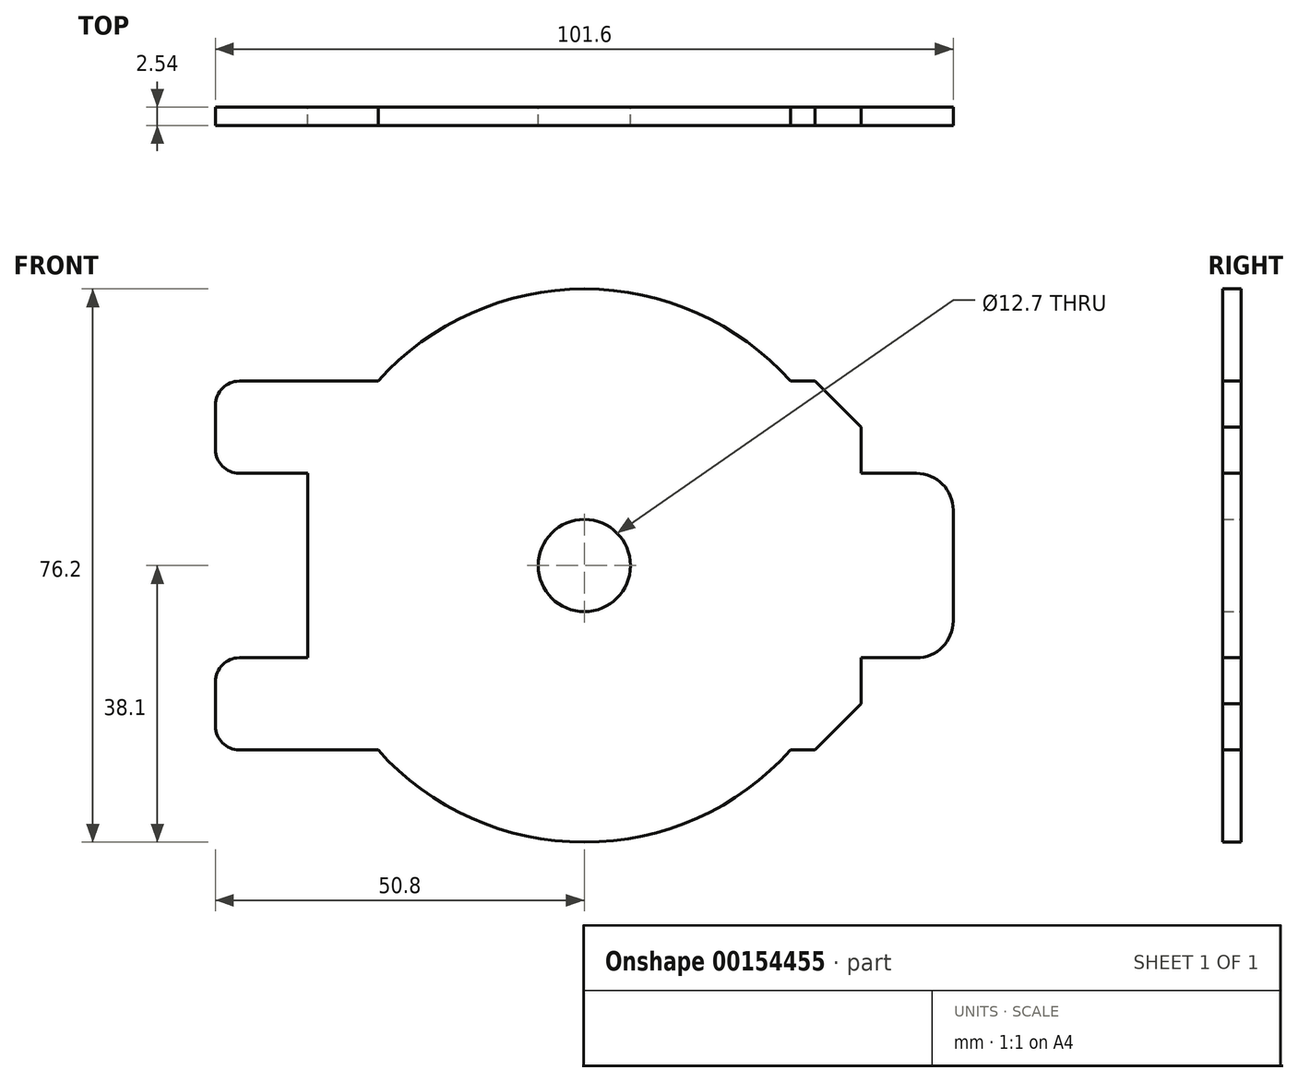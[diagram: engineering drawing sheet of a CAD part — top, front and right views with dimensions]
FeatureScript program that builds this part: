
annotation { "Feature Type Name" : "Feature", "Feature Type Description" : "" }
export const myFeature = defineFeature(function(context is Context, id is Id, definition is map)
    precondition{}
    {
        {
            var Q0;
            Q0=qCreatedBy(makeId("Front.planeOp"),FACE);
            var sketch = newSketch(context, id + "F0", { "sketchPlane" : qUnion([Q0])});
            skLineSegment(sketch, "E0.bottom", {"start": v(38.1, 25.4) * mm, "end": v(28.4, 25.4) * mm});
            skLineSegment(sketch, "E0.top", {"start": v(38.1, -25.4) * mm, "end": v(28.4, -25.4) * mm});
            skLineSegment(sketch, "E0.left", {"start": v(38.1, 25.4) * mm, "end": v(38.1, -25.4) * mm});
            skLineSegment(sketch, "E0.right", {"start": v(-38.1, 25.4) * mm, "end": v(-38.1, -25.4) * mm});
            skPoint(sketch, "E0.middle", {"position": v(0, 0) * mm});
            skArc(sketch, "E1", {"start": v(-28.4, -25.4) * mm, "mid": v(0, -38.1) * mm, "end": v(28.4, -25.4) * mm});
            skLineSegment(sketch, "E2.trimOffspring", {"start": v(-28.4, 25.4) * mm, "end": v(-38.1, 25.4) * mm});
            skLineSegment(sketch, "E3.trimOffspring", {"start": v(-28.4, -25.4) * mm, "end": v(-38.1, -25.4) * mm});
            skArc(sketch, "E4.trimOffspring", {"start": v(28.4, 25.4) * mm, "mid": v(0, 38.1) * mm, "end": v(-28.4, 25.4) * mm});
            skLineSegment(sketch, "E5.bottom", {"start": v(38.1, 12.7) * mm, "end": v(50.8, 12.7) * mm});
            skLineSegment(sketch, "E5.top", {"start": v(38.1, -12.7) * mm, "end": v(50.8, -12.7) * mm});
            skLineSegment(sketch, "E5.right", {"start": v(50.8, 12.7) * mm, "end": v(50.8, -12.7) * mm});
            skPoint(sketch, "E5.middle", {"position": v(38.1, 0) * mm});
            skPoint(sketch, "E5.left.start.orphan", {"position": v(25.4, 12.7) * mm});
            skPoint(sketch, "E6.orphan", {"position": v(25.4, -12.7) * mm});
            skPoint(sketch, "E7.MirrorCS.end.orphan", {"position": v(-25.4, -12.7) * mm});
            skPoint(sketch, "E7.MirrorCS.start.orphan", {"position": v(-25.4, 12.7) * mm});
            skPoint(sketch, "E8.MirrorCS.end.orphan", {"position": v(-50.8, 12.7) * mm});
            skPoint(sketch, "E9.MirrorCS.end.orphan", {"position": v(-50.8, -12.7) * mm});
            skLineSegment(sketch, "E10.bottom", {"start": v(-38.1, -25.4) * mm, "end": v(-50.8, -25.4) * mm});
            skLineSegment(sketch, "E10.top", {"start": v(-38.1, -12.7) * mm, "end": v(-50.8, -12.7) * mm});
            skLineSegment(sketch, "E10.left", {"start": v(-38.1, -25.4) * mm, "end": v(-38.1, -12.7) * mm});
            skLineSegment(sketch, "E10.right", {"start": v(-50.8, -25.4) * mm, "end": v(-50.8, -12.7) * mm});
            skLineSegment(sketch, "E11.MirrorCS", {"start": v(-38.1, 12.7) * mm, "end": v(-50.8, 12.7) * mm});
            skLineSegment(sketch, "E12.MirrorCS", {"start": v(-38.1, 25.4) * mm, "end": v(-50.8, 25.4) * mm});
            skLineSegment(sketch, "E13.MirrorCS", {"start": v(-50.8, 25.4) * mm, "end": v(-50.8, 12.7) * mm});
            skSolve(sketch);
        }
        {
            var Q0;
            Q0 = qSketchRegion(id + "F0", true);
            extrude(context, id + "F1", {"entities" : qUnion([Q0]), "depth" : 2.54 * mm});
        }
        {
            var Q0;
            Q0=makeQuery(id+"F1.opExtrude","CAP_FACE",FACE,{"disambiguationData":[OSD([sQuery(id+"F0.wireOp",EDGE,"E0.bottom"),sQuery(id+"F0.wireOp",EDGE,"E0.top"),sQuery(id+"F0.wireOp",EDGE,"E0.left"),sQuery(id+"F0.wireOp",EDGE,"E0.right")])],"isStart":false});
            var sketch = newSketch(context, id + "F2", { "sketchPlane" : qUnion([Q0])});
            skSolve(sketch);
        }
        {
            var Q0;
            Q0=makeQuery(id+"F2.imprint","IMPRINT",FACE,{"disambiguationData":[TD([[makeQuery(id+"F2.imprint","IMPRINT",EDGE,{"derivedFrom":makeQuery(id+"F1.opExtrude","CAP_EDGE",EDGE,{"disambiguationData":[OSD([sQuery(id+"F0.wireOp",EDGE,"E0.bottom")])],"isStart":false})}),1.0]])]});
            var sketch = newSketch(context, id + "F3", { "sketchPlane" : qUnion([Q0])});
            skCircle(sketch, "E14", {"center": v(0, 0) * mm, "radius": 6.35 * mm});
            skSolve(sketch);
        }
        {
            var Q0;
            Q0 = qSketchRegion(id + "F3", true);
            extrude(context, id + "F4", {"entities" : qUnion([Q0]), "operationType" : NewBodyOperationType.REMOVE, "endBound" : BoundingType.SYMMETRIC, "depth" : 25.4 * mm});
        }
        {
            var Q0;
            Q0=makeQuery(id+"F1.opExtrude","SWEPT_EDGE",EDGE,{"disambiguationData":[OSD([sQuery(id+"F0.wireOp",EDGE,"E0.bottom"),sQuery(id+"F0.wireOp",EDGE,"E0.left")])]});
            chamfer(context, id + "F5", {"entities" : qUnion([Q0]), "width" : 6.35 * mm, "tangentPropagation" : true});
        }
        {
            var Q0;
            Q0=makeQuery(id+"F1.opExtrude","SWEPT_EDGE",EDGE,{"disambiguationData":[OSD([sQuery(id+"F0.wireOp",EDGE,"E0.top"),sQuery(id+"F0.wireOp",EDGE,"E0.left")])]});
            chamfer(context, id + "F6", {"entities" : qUnion([Q0]), "width" : 6.35 * mm, "tangentPropagation" : true});
        }
        {
            var Q0;
            Q0=makeQuery(id+"F1.opExtrude","SWEPT_EDGE",EDGE,{"disambiguationData":[OSD([sQuery(id+"F0.wireOp",EDGE,"E5.bottom"),sQuery(id+"F0.wireOp",EDGE,"E5.right")])]});
            var Q1;
            Q1=makeQuery(id+"F1.opExtrude","SWEPT_EDGE",EDGE,{"disambiguationData":[OSD([sQuery(id+"F0.wireOp",EDGE,"E5.top"),sQuery(id+"F0.wireOp",EDGE,"E5.right")])]});
            fillet(context, id + "F7", {"entities" : qUnion([Q0, Q1]), "radius" : 5.08 * mm, "tangentPropagation" : true, "allowEdgeOverflow" : false});
        }
        {
            var Q0;
            Q0=makeQuery(id+"F1.opExtrude","SWEPT_EDGE",EDGE,{"disambiguationData":[OSD([sQuery(id+"F0.wireOp",EDGE,"E12.MirrorCS"),sQuery(id+"F0.wireOp",EDGE,"E13.MirrorCS")])]});
            var Q1;
            Q1=makeQuery(id+"F1.opExtrude","SWEPT_EDGE",EDGE,{"disambiguationData":[OSD([sQuery(id+"F0.wireOp",EDGE,"E11.MirrorCS"),sQuery(id+"F0.wireOp",EDGE,"E13.MirrorCS")])]});
            var Q2;
            Q2=makeQuery(id+"F1.opExtrude","SWEPT_EDGE",EDGE,{"disambiguationData":[OSD([sQuery(id+"F0.wireOp",EDGE,"E10.bottom"),sQuery(id+"F0.wireOp",EDGE,"E10.right")])]});
            var Q3;
            Q3=makeQuery(id+"F1.opExtrude","SWEPT_EDGE",EDGE,{"disambiguationData":[OSD([sQuery(id+"F0.wireOp",EDGE,"E10.top"),sQuery(id+"F0.wireOp",EDGE,"E10.right")])]});
            fillet(context, id + "F8", {"entities" : qUnion([Q0, Q1, Q2, Q3]), "radius" : 3.3 * mm, "tangentPropagation" : true, "allowEdgeOverflow" : false});
        }
    });
